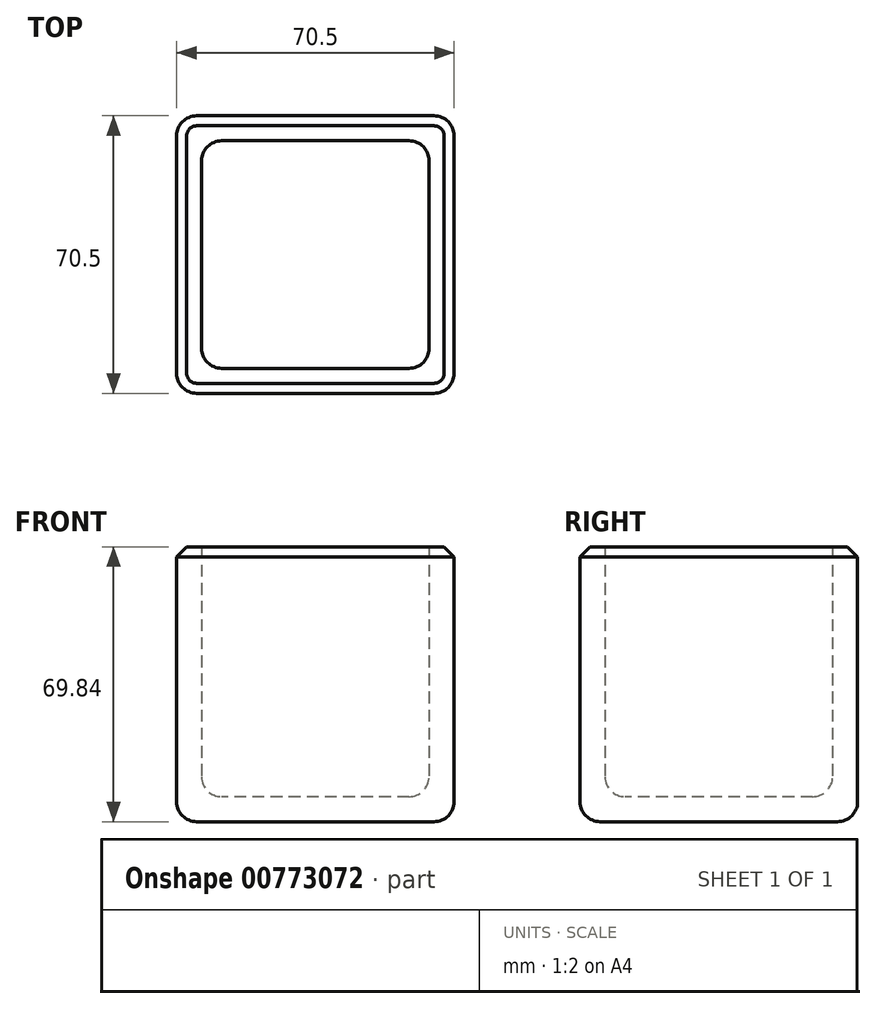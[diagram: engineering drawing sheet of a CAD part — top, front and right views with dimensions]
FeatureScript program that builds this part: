
annotation { "Feature Type Name" : "Feature", "Feature Type Description" : "" }
export const myFeature = defineFeature(function(context is Context, id is Id, definition is map)
    precondition{}
    {
        {
            var Q0;
            Q0=qCreatedBy(makeId("Top.planeOp"),FACE);
            var sketch = newSketch(context, id + "F0", { "sketchPlane" : qUnion([Q0])});
            skLineSegment(sketch, "E0.bottom", {"start": v(35.25, 35.25) * mm, "end": v(-35.25, 35.25) * mm});
            skLineSegment(sketch, "E0.top", {"start": v(35.25, -35.25) * mm, "end": v(-35.25, -35.25) * mm});
            skLineSegment(sketch, "E0.left", {"start": v(35.25, 35.25) * mm, "end": v(35.25, -35.25) * mm});
            skLineSegment(sketch, "E0.right", {"start": v(-35.25, 35.25) * mm, "end": v(-35.25, -35.25) * mm});
            skPoint(sketch, "E0.middle", {"position": v(0, 0) * mm});
            skSolve(sketch);
        }
        {
            var Q0;
            Q0=makeQuery(id+"F0.imprint","IMPRINT",FACE,{"disambiguationData":[TD([[makeQuery(id+"F0.imprint","IMPRINT",EDGE,{"derivedFrom":sQuery(id+"F0.wireOp",EDGE,"E0.bottom")}),1.0]])]});
            extrude(context, id + "F1", {"entities" : qUnion([Q0]), "endBound" : BoundingType.SYMMETRIC, "depth" : 69.85 * mm, "offsetDistance" : 25.4 * mm});
        }
        {
            var Q0;
            Q0=makeQuery(id+"F1.opExtrude","CAP_FACE",FACE,{"disambiguationData":[OSD([sQuery(id+"F0.wireOp",EDGE,"E0.bottom"),sQuery(id+"F0.wireOp",EDGE,"E0.top"),sQuery(id+"F0.wireOp",EDGE,"E0.left"),sQuery(id+"F0.wireOp",EDGE,"E0.right")])],"isStart":false});
            shell(context, id + "F2", {"entities" : qUnion([Q0]), "thickness" : 6.35 * mm});
        }
        {
            var Q0;
            Q0=makeQuery(id+"F1.opExtrude","CAP_EDGE",EDGE,{"disambiguationData":[OSD([sQuery(id+"F0.wireOp",EDGE,"E0.bottom")])],"isStart":true});
            var Q1;
            Q1=makeQuery(id+"F1.opExtrude","CAP_EDGE",EDGE,{"disambiguationData":[OSD([sQuery(id+"F0.wireOp",EDGE,"E0.top")])],"isStart":true});
            var Q2;
            Q2=makeQuery(id+"F1.opExtrude","CAP_EDGE",EDGE,{"disambiguationData":[OSD([sQuery(id+"F0.wireOp",EDGE,"E0.left")])],"isStart":true});
            var Q3;
            Q3=makeQuery(id+"F1.opExtrude","CAP_EDGE",EDGE,{"disambiguationData":[OSD([sQuery(id+"F0.wireOp",EDGE,"E0.right")])],"isStart":true});
            var Q4;
            {var subQ0=sQuery(id+"F0.wireOp",EDGE,"E0.top");Q4=makeQuery(id+"F2.opShell","OFFSET_EDGE",EDGE,{"disambiguationData":[OSD([subQ0]),TDD([makeQuery(id+"F1.opExtrude","CAP_EDGE",EDGE,{"disambiguationData":[OSD([subQ0])],"isStart":true})])]});}
            var Q5;
            {var subQ0=sQuery(id+"F0.wireOp",EDGE,"E0.left");Q5=makeQuery(id+"F2.opShell","OFFSET_EDGE",EDGE,{"disambiguationData":[OSD([subQ0]),TDD([makeQuery(id+"F1.opExtrude","CAP_EDGE",EDGE,{"disambiguationData":[OSD([subQ0])],"isStart":true})])]});}
            var Q6;
            {var subQ0=sQuery(id+"F0.wireOp",EDGE,"E0.right");Q6=makeQuery(id+"F2.opShell","OFFSET_EDGE",EDGE,{"disambiguationData":[OSD([subQ0]),TDD([makeQuery(id+"F1.opExtrude","CAP_EDGE",EDGE,{"disambiguationData":[OSD([subQ0])],"isStart":true})])]});}
            var Q7;
            {var subQ0=sQuery(id+"F0.wireOp",EDGE,"E0.bottom");Q7=makeQuery(id+"F2.opShell","OFFSET_EDGE",EDGE,{"disambiguationData":[OSD([subQ0]),TDD([makeQuery(id+"F1.opExtrude","CAP_EDGE",EDGE,{"disambiguationData":[OSD([subQ0])],"isStart":true})])]});}
            var Q8;
            Q8=makeQuery(id+"F1.opExtrude","SWEPT_EDGE",EDGE,{"disambiguationData":[OSD([sQuery(id+"F0.wireOp",EDGE,"E0.top"),sQuery(id+"F0.wireOp",EDGE,"E0.left")])]});
            var Q9;
            Q9=makeQuery(id+"F1.opExtrude","SWEPT_EDGE",EDGE,{"disambiguationData":[OSD([sQuery(id+"F0.wireOp",EDGE,"E0.bottom"),sQuery(id+"F0.wireOp",EDGE,"E0.left")])]});
            var Q10;
            Q10=makeQuery(id+"F1.opExtrude","SWEPT_EDGE",EDGE,{"disambiguationData":[OSD([sQuery(id+"F0.wireOp",EDGE,"E0.bottom"),sQuery(id+"F0.wireOp",EDGE,"E0.right")])]});
            var Q11;
            Q11=makeQuery(id+"F1.opExtrude","SWEPT_EDGE",EDGE,{"disambiguationData":[OSD([sQuery(id+"F0.wireOp",EDGE,"E0.top"),sQuery(id+"F0.wireOp",EDGE,"E0.right")])]});
            var Q12;
            Q12=makeQuery(id+"F2.opShell","OFFSET_EDGE",EDGE,{"disambiguationData":[OSD([sQuery(id+"F0.wireOp",EDGE,"E0.bottom"),sQuery(id+"F0.wireOp",EDGE,"E0.right")])]});
            var Q13;
            Q13=makeQuery(id+"F2.opShell","OFFSET_EDGE",EDGE,{"disambiguationData":[OSD([sQuery(id+"F0.wireOp",EDGE,"E0.bottom"),sQuery(id+"F0.wireOp",EDGE,"E0.left")])]});
            var Q14;
            Q14=makeQuery(id+"F2.opShell","OFFSET_EDGE",EDGE,{"disambiguationData":[OSD([sQuery(id+"F0.wireOp",EDGE,"E0.top"),sQuery(id+"F0.wireOp",EDGE,"E0.left")])]});
            var Q15;
            Q15=makeQuery(id+"F2.opShell","OFFSET_EDGE",EDGE,{"disambiguationData":[OSD([sQuery(id+"F0.wireOp",EDGE,"E0.top"),sQuery(id+"F0.wireOp",EDGE,"E0.right")])]});
            fillet(context, id + "F3", {"entities" : qUnion([Q0, Q1, Q2, Q3, Q4, Q5, Q6, Q7, Q8, Q9, Q10, Q11, Q12, Q13, Q14, Q15]), "radius" : 5.08 * mm, "tangentPropagation" : true, "allowEdgeOverflow" : false});
        }
        {
            var Q0;
            Q0=makeQuery(id+"F1.opExtrude","CAP_EDGE",EDGE,{"disambiguationData":[OSD([sQuery(id+"F0.wireOp",EDGE,"E0.right")])],"isStart":false});
            chamfer(context, id + "F4", {"entities" : qUnion([Q0]), "width" : 2.54 * mm, "tangentPropagation" : true});
        }
    });
